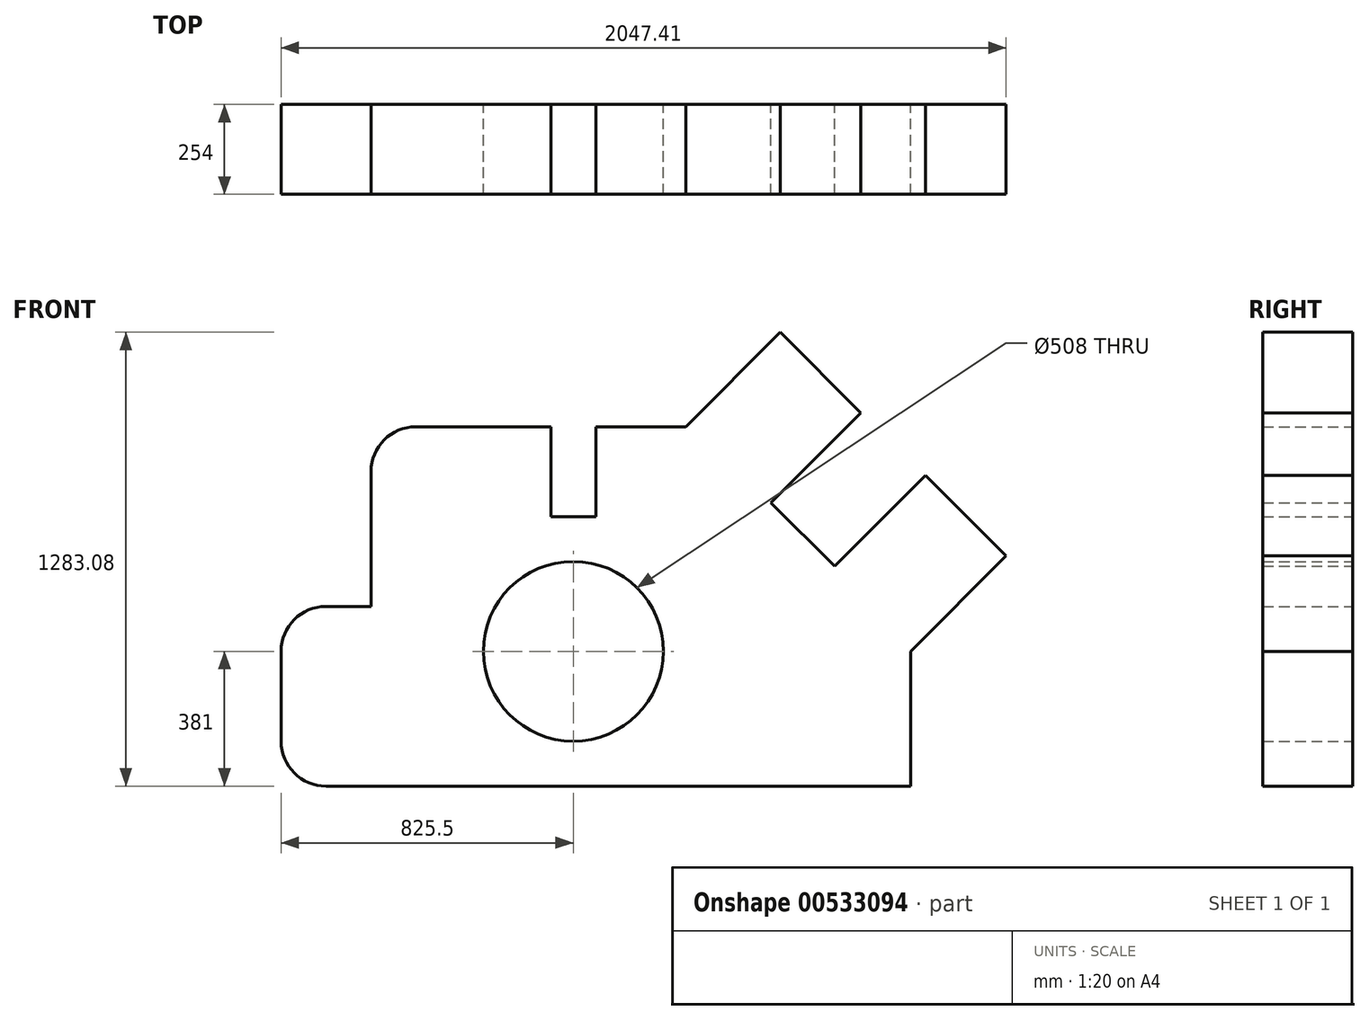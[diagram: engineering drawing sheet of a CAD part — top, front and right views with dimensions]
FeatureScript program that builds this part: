
annotation { "Feature Type Name" : "Feature", "Feature Type Description" : "" }
export const myFeature = defineFeature(function(context is Context, id is Id, definition is map)
    precondition{}
    {
        {
            var Q0;
            Q0=qCreatedBy(makeId("Front.planeOp"),FACE);
            var sketch = newSketch(context, id + "F0", { "sketchPlane" : qUnion([Q0])});
            skLineSegment(sketch, "E0", {"start": v(127, 0) * mm, "end": v(1778, 0) * mm});
            skLineSegment(sketch, "E1", {"start": v(1778, 0) * mm, "end": v(1778, 381) * mm});
            skLineSegment(sketch, "E2", {"start": v(0, 127) * mm, "end": v(0, 381) * mm});
            skCircle(sketch, "E3", {"center": v(825.5, 381) * mm, "radius": 254 * mm});
            skLineSegment(sketch, "E4", {"start": v(127, 508) * mm, "end": v(254, 508) * mm});
            skLineSegment(sketch, "E5", {"start": v(254, 508) * mm, "end": v(254, 889) * mm});
            skLineSegment(sketch, "E6", {"start": v(381, 1016) * mm, "end": v(762, 1016) * mm});
            skLineSegment(sketch, "E7", {"start": v(762, 1016) * mm, "end": v(762, 762) * mm});
            skLineSegment(sketch, "E8", {"start": v(762, 762) * mm, "end": v(889, 762) * mm});
            skLineSegment(sketch, "E9", {"start": v(889, 762) * mm, "end": v(889, 1016) * mm});
            skLineSegment(sketch, "E10", {"start": v(889, 1016) * mm, "end": v(1143, 1016) * mm});
            skLineSegment(sketch, "E11", {"start": v(1778, 381) * mm, "end": v(2047.4, 650.4) * mm});
            skLineSegment(sketch, "E12", {"start": v(2047.4, 650.4) * mm, "end": v(1819.71, 878.1) * mm});
            skLineSegment(sketch, "E13", {"start": v(1819.71, 878.1) * mm, "end": v(1563.46, 621.85) * mm});
            skLineSegment(sketch, "E14", {"start": v(1563.46, 621.85) * mm, "end": v(1383.85, 801.46) * mm});
            skLineSegment(sketch, "E15", {"start": v(1383.85, 801.46) * mm, "end": v(1637.77, 1055.38) * mm});
            skLineSegment(sketch, "E16", {"start": v(1637.77, 1055.38) * mm, "end": v(1410.08, 1283.08) * mm});
            skLineSegment(sketch, "E17", {"start": v(1410.08, 1283.08) * mm, "end": v(1143, 1016) * mm});
            skPoint(sketch, "E18.visualSharp", {"position": v(0, 508) * mm});
            skArc(sketch, "E18.filletArc", {"start": v(127, 508) * mm, "mid": v(37.2, 470.8) * mm, "end": v(0, 381) * mm});
            skPoint(sketch, "E19.visualSharp", {"position": v(0, 0) * mm});
            skArc(sketch, "E19.filletArc", {"start": v(0, 127) * mm, "mid": v(37.2, 37.2) * mm, "end": v(127, 0) * mm});
            skPoint(sketch, "E20.visualSharp", {"position": v(254, 1016) * mm});
            skArc(sketch, "E20.filletArc", {"start": v(381, 1016) * mm, "mid": v(291.2, 978.8) * mm, "end": v(254, 889) * mm});
            skSolve(sketch);
        }
        {
            var Q0;
            Q0=makeQuery(id+"F0.imprint","IMPRINT",FACE,{"disambiguationData":[TD([[makeQuery(id+"F0.imprint","IMPRINT",EDGE,{"derivedFrom":sQuery(id+"F0.wireOp",EDGE,"E0")}),1.0]])]});
            extrude(context, id + "F1", {"entities" : qUnion([Q0]), "depth" : 254 * mm, "offsetDistance" : 25.4 * mm});
        }
    });
